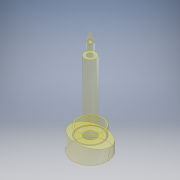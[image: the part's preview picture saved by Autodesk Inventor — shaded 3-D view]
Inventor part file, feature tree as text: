
AUTODESK INVENTOR PART (.ipt)
format: ipt  version: 2017 (Build 210142000, 142)  size: 158,208 bytes
history: native  units: mm
features: sketch x7, extrude x3, plane x2, loft x2, other x1
ambient origin geometry x8: Origin, YZ Plane, XZ Plane, XY Plane, X Axis, Y Axis, Z Axis, Center Point
bodies: Body1 (feature_tree)
feature tree (15):
  sketch  "Sketch1"  dims[d0=15.0mm d7=0.0mm d8=90.0deg]
  plane  "Work Plane1"
  loft  "Loft1"
  extrude  "Extrusion2"  Depth=10.0mm
  extrude  "Extrusion3"  Depth=4.0mm TaperAngle=0.0deg
  extrude  "Extrusion4"  Depth=30.0mm TaperAngle=0.0deg
  sketch  "Sketch6"  dims[d21=5.0mm]
  plane  "Work Plane2"
  loft  "Loft2"
  sketch  "Sketch2"  dims[d9=0.0mm d10=90.0deg d11=10.0mm]
  sketch  "Sketch3"  dims[d12=11.0mm d13=4.0mm d14=0.0mm]
  sketch  "Sketch4"  dims[d15=5.0mm d16=30.0mm d17=0.0mm]
  sketch  "Sketch5"  dims[d18=2.5mm d19=5.0mm d20=0.0mm]
  sketch  "Sketch7"  dims[d22=0.0mm d23=90.0deg d24=0.0mm d25=90.0deg d26=7.5mm]
  other  "Edges1"
